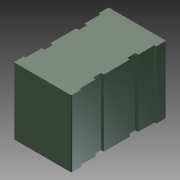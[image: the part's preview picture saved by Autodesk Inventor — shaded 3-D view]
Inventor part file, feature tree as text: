
AUTODESK INVENTOR PART (.ipt)
format: ipt  version: 2014 (Build 180170000, 170)  size: 160,256 bytes
history: native  units: in
note: dims shown in document units (in); Inventor stores cm internally (conversion verified against a paired STEP export)
features: other x21, extrude x3, sketch x3, pattern_linear x1
ambient origin geometry x8: Origin, YZ Plane, XZ Plane, XY Plane, X Axis, Y Axis, Z Axis, Center Point
bodies: Solid1 (feature_tree)
feature tree (28):
  extrude  "Extrusion1"  Depth=0.001in TaperAngle=0.0deg
  extrude  "Extrusion2"  Depth=0.185in TaperAngle=0.0deg
  extrude  "Extrusion3"  [1 undecoded]
  pattern_linear  "Rectangular Pattern1"  [2 undecoded]
  other  "rot_XY"
  other  "rot_YZ"
  other  "rot_ZX"
  other  "rot_X"
  other  "rot_Y"
  other  "rot_Z"
  other  "rot_Center"
  other  "to_cover_XY"
  other  "to_cover_YZ"
  other  "to_cover_ZX"
  other  "to_cover_X"
  other  "to_cover_Y"
  other  "to_cover_Z"
  other  "to_cover_Center"
  other  "to_terminals_XY"
  other  "to_terminals_YZ"
  other  "to_terminals_ZX"
  other  "to_terminals_X"
  other  "to_terminals_Y"
  other  "to_terminals_Z"
  other  "to_terminals_Center"
  sketch  "Sketch_2"  dims[d4=0.01in d5=0.0in d6=1.1811in d8=0.185in d9=0.3937in d11=0.0in]
  sketch  "Sketch_1"  dims[d0=0.361in d1=0.0in d2=0.001in d3=0.0in]
  sketch  "Sketch_7"
note: 3 required parameter values undecoded (feature->parameter linkage not recoverable at this tier; creation-order binding heuristic only, values carry confidence <= 0.55)
